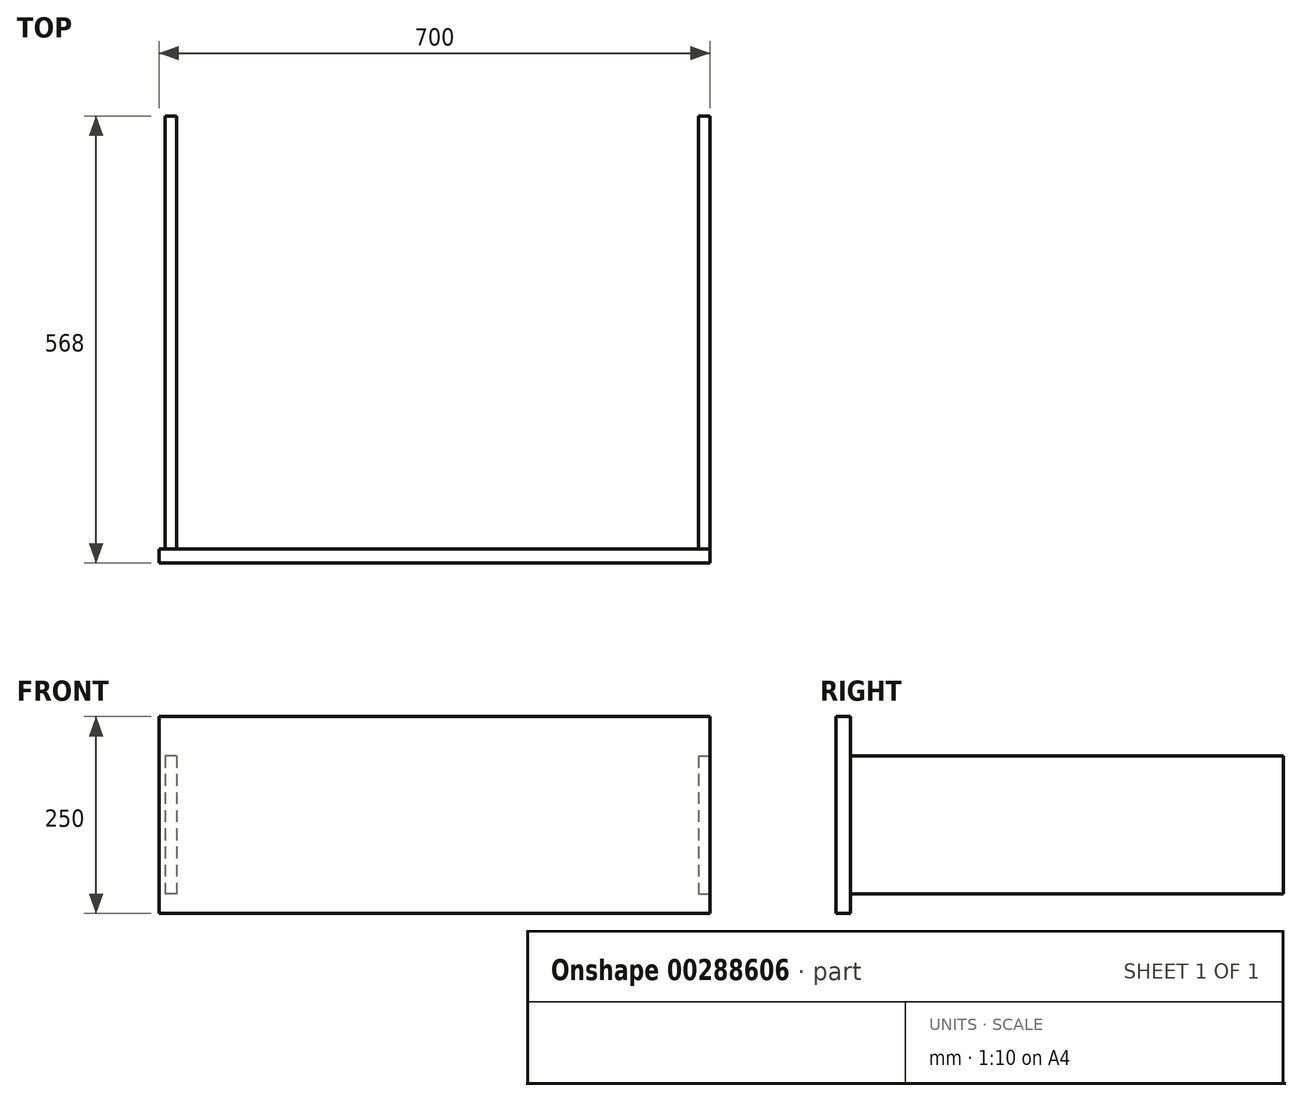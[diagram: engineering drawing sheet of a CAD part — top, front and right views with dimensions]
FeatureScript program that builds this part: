
annotation { "Feature Type Name" : "Feature", "Feature Type Description" : "" }
export const myFeature = defineFeature(function(context is Context, id is Id, definition is map)
    precondition{}
    {
        {
            var Q0;
            Q0=qCreatedBy(makeId("Front.planeOp"),FACE);
            var sketch = newSketch(context, id + "F0", { "sketchPlane" : qUnion([Q0])});
            skLineSegment(sketch, "E0.bottom", {"start": v(-353.67, 135.48) * mm, "end": v(346.33, 135.48) * mm});
            skLineSegment(sketch, "E0.top", {"start": v(-353.67, -114.52) * mm, "end": v(346.33, -114.52) * mm});
            skLineSegment(sketch, "E0.left", {"start": v(-353.67, 135.48) * mm, "end": v(-353.67, -114.52) * mm});
            skLineSegment(sketch, "E0.right", {"start": v(346.33, 135.48) * mm, "end": v(346.33, -114.52) * mm});
            skSolve(sketch);
        }
        {
            var Q0;
            Q0 = qSketchRegion(id + "F0", true);
            extrude(context, id + "F1", {"entities" : qUnion([Q0]), "depth" : 18 * mm});
        }
        {
            var Q0;
            Q0=makeQuery(id+"F1.opExtrude","SWEPT_FACE",FACE,{"disambiguationData":[OSD([sQuery(id+"F0.wireOp",EDGE,"E0.right")])]});
            var sketch = newSketch(context, id + "F2", { "sketchPlane" : qUnion([Q0])});
            skLineSegment(sketch, "E1.bottom", {"start": v(0, 85.48) * mm, "end": v(550, 85.48) * mm});
            skLineSegment(sketch, "E1.top", {"start": v(0, -114.52) * mm, "end": v(550, -114.52) * mm});
            skLineSegment(sketch, "E1.left", {"start": v(0, 85.48) * mm, "end": v(0, -114.52) * mm});
            skLineSegment(sketch, "E1.right", {"start": v(550, 85.48) * mm, "end": v(550, -114.52) * mm});
            skSolve(sketch);
        }
        {
            var Q0;
            Q0 = qSketchRegion(id + "F2", true);
            extrude(context, id + "F3", {"entities" : qUnion([Q0]), "oppositeDirection" : true, "depth" : 15 * mm});
        }
        {
            var Q0;
            Q0=makeQuery(id+"F3.opExtrude","SWEPT_FACE",FACE,{"disambiguationData":[OSD([sQuery(id+"F2.wireOp",EDGE,"E1.top")])]});
            extrude(context, id + "F4", {"entities" : qUnion([Q0]), "operationType" : NewBodyOperationType.REMOVE, "oppositeDirection" : true, "depth" : 25 * mm});
        }
        {
            var Q0;
            Q0=makeQuery(id+"F3.opExtrude","SWEPT_BODY",BODY,{"disambiguationData":[OSD([sQuery(id+"F2.wireOp",EDGE,"E1.bottom"),sQuery(id+"F2.wireOp",EDGE,"E1.top"),sQuery(id+"F2.wireOp",EDGE,"E1.left"),sQuery(id+"F2.wireOp",EDGE,"E1.right")])]});
            var Q1;
            Q1=qCreatedBy(makeId("Right.planeOp"),FACE);
            mirror(context, id + "F5", {"entities" : qUnion([Q0]), "mirrorPlane" : qUnion([Q1])});
        }
    });
